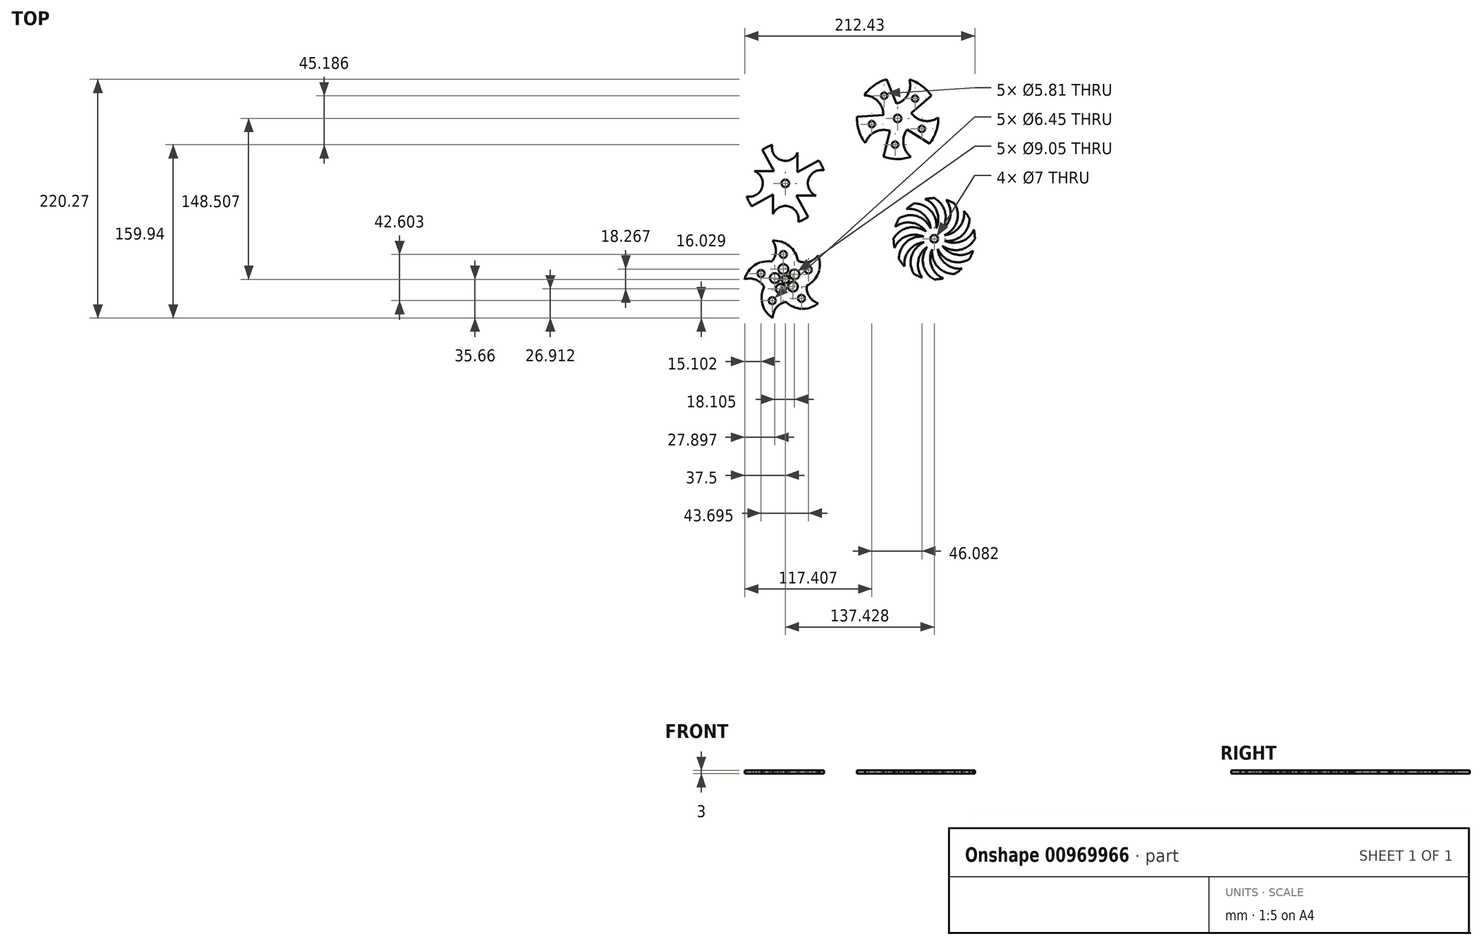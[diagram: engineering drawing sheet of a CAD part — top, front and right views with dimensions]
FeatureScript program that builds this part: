
annotation { "Feature Type Name" : "Feature", "Feature Type Description" : "" }
export const myFeature = defineFeature(function(context is Context, id is Id, definition is map)
    precondition{}
    {
        {
            var Q0;
            Q0=qCreatedBy(makeId("Top.planeOp"),FACE);
            var sketch = newSketch(context, id + "F0", { "sketchPlane" : qUnion([Q0])});
            skLineSegment(sketch, "E0.bottom", {"start": v(37.5, -37.5) * mm, "end": v(-37.5, -37.5) * mm});
            skLineSegment(sketch, "E0.top", {"start": v(37.5, 37.5) * mm, "end": v(-37.5, 37.5) * mm});
            skLineSegment(sketch, "E0.left", {"start": v(37.5, -37.5) * mm, "end": v(37.5, 37.5) * mm});
            skLineSegment(sketch, "E0.right", {"start": v(-37.5, -37.5) * mm, "end": v(-37.5, 37.5) * mm});
            skPoint(sketch, "E0.middle", {"position": v(0, 0) * mm});
            skCircle(sketch, "E1", {"center": v(0, 0) * mm, "radius": 3.5 * mm});
            skCircle(sketch, "E2", {"center": v(0, 0) * mm, "radius": 37.5 * mm});
            skArc(sketch, "E3", {"start": v(-12.52, 16.37) * mm, "mid": v(-28.22, 13.08) * mm, "end": v(-37.5, 0) * mm});
            skArc(sketch, "E4", {"start": v(-20.17, -5.87) * mm, "mid": v(-27.84, -0.01) * mm, "end": v(-37.5, 0) * mm});
            skArc(sketch, "E5", {"start": v(-20.17, -5.87) * mm, "mid": v(-19.82, -6.37) * mm, "end": v(-19.44, -6.85) * mm});
            skCircle(sketch, "E6", {"center": v(-9.6, 1.25) * mm, "radius": 4.53 * mm});
            skCircle(sketch, "E7", {"center": v(-22.4, 5.4) * mm, "radius": 3.23 * mm});
            skArc(sketch, "E8.1.0", {"start": v(-0.65, -21) * mm, "mid": v(-8.6, -26.48) * mm, "end": v(-11.59, -35.66) * mm});
            skArc(sketch, "E8.1.1", {"start": v(-19.44, -6.85) * mm, "mid": v(-21.16, -22.8) * mm, "end": v(-11.59, -35.66) * mm});
            skArc(sketch, "E8.1.2", {"start": v(-0.65, -21) * mm, "mid": v(-0.06, -20.81) * mm, "end": v(0.51, -20.6) * mm});
            skCircle(sketch, "E8.1.3", {"center": v(-12.06, -19.63) * mm, "radius": 3.23 * mm});
            skCircle(sketch, "E8.1.4", {"center": v(-4.15, -8.75) * mm, "radius": 4.53 * mm});
            skArc(sketch, "E8.2.0", {"start": v(19.77, -7.1) * mm, "mid": v(22.53, -16.36) * mm, "end": v(30.34, -22.04) * mm});
            skArc(sketch, "E8.2.1", {"start": v(0.51, -20.6) * mm, "mid": v(15.14, -27.17) * mm, "end": v(30.34, -22.04) * mm});
            skArc(sketch, "E8.2.2", {"start": v(19.77, -7.1) * mm, "mid": v(19.78, -6.5) * mm, "end": v(19.75, -5.88) * mm});
            skCircle(sketch, "E8.2.3", {"center": v(14.94, -17.54) * mm, "radius": 3.23 * mm});
            skCircle(sketch, "E8.2.4", {"center": v(7.04, -6.65) * mm, "radius": 4.53 * mm});
            skArc(sketch, "E8.3.0", {"start": v(12.86, 16.6) * mm, "mid": v(22.52, 16.38) * mm, "end": v(30.34, 22.04) * mm});
            skArc(sketch, "E8.3.1", {"start": v(19.75, -5.88) * mm, "mid": v(30.52, 6) * mm, "end": v(30.34, 22.04) * mm});
            skArc(sketch, "E8.3.2", {"start": v(12.86, 16.6) * mm, "mid": v(12.29, 16.8) * mm, "end": v(11.7, 16.97) * mm});
            skCircle(sketch, "E8.3.3", {"center": v(21.3, 8.8) * mm, "radius": 3.23 * mm});
            skCircle(sketch, "E8.3.4", {"center": v(8.5, 4.64) * mm, "radius": 4.53 * mm});
            skArc(sketch, "E8.4.0", {"start": v(-11.82, 17.37) * mm, "mid": v(-8.62, 26.48) * mm, "end": v(-11.59, 35.66) * mm});
            skArc(sketch, "E8.4.1", {"start": v(11.7, 16.97) * mm, "mid": v(3.72, 30.88) * mm, "end": v(-11.59, 35.66) * mm});
            skArc(sketch, "E8.4.2", {"start": v(-11.82, 17.37) * mm, "mid": v(-12.18, 16.88) * mm, "end": v(-12.52, 16.37) * mm});
            skCircle(sketch, "E8.4.3", {"center": v(-1.78, 22.97) * mm, "radius": 3.23 * mm});
            skCircle(sketch, "E8.4.4", {"center": v(-1.78, 9.52) * mm, "radius": 4.53 * mm});
            skPoint(sketch, "E9.orphan", {"position": v(-16.02, -2.03) * mm});
            skPoint(sketch, "E10.orphan", {"position": v(-6.88, 14.61) * mm});
            skPoint(sketch, "E11.orphan", {"position": v(-3.02, -15.87) * mm});
            skPoint(sketch, "E12.orphan", {"position": v(-0.8, 13.34) * mm});
            skPoint(sketch, "E13.orphan", {"position": v(12.44, 4.89) * mm});
            skPoint(sketch, "E14.orphan", {"position": v(14.16, -7.77) * mm});
            skPoint(sketch, "E15.orphan", {"position": v(11.77, 11.06) * mm});
            skSolve(sketch);
        }
        {
            var Q0;
            Q0=makeQuery(id+"F0.imprint","IMPRINT",FACE,{"disambiguationData":[TD([[makeQuery(id+"F0.imprint","IMPRINT",EDGE,{"derivedFrom":sQuery(id+"F0.wireOp",EDGE,"E1")}),-1.0]])]});
            extrude(context, id + "F1", {"entities" : qUnion([Q0]), "depth" : 3 * mm, "offsetDistance" : 25 * mm});
        }
        {
            var Q0;
            Q0=qCreatedBy(makeId("Top.planeOp"),FACE);
            var sketch = newSketch(context, id + "F2", { "sketchPlane" : qUnion([Q0])});
            skLineSegment(sketch, "E16.bottom", {"start": v(37.5, 126.08) * mm, "end": v(-37.5, 126.08) * mm});
            skLineSegment(sketch, "E16.top", {"start": v(37.5, 51.08) * mm, "end": v(-37.5, 51.08) * mm});
            skLineSegment(sketch, "E16.left", {"start": v(37.5, 126.08) * mm, "end": v(37.5, 51.08) * mm});
            skLineSegment(sketch, "E16.right", {"start": v(-37.5, 126.08) * mm, "end": v(-37.5, 51.08) * mm});
            skPoint(sketch, "E16.middle", {"position": v(0, 88.58) * mm});
            skCircle(sketch, "E17", {"center": v(0, 88.58) * mm, "radius": 37.5 * mm});
            skCircle(sketch, "E18", {"center": v(0, 88.58) * mm, "radius": 3.5 * mm});
            skArc(sketch, "E19", {"start": v(-12.02, 124.1) * mm, "mid": v(-3.55, 109.91) * mm, "end": v(11.36, 117.03) * mm});
            skLineSegment(sketch, "E20", {"start": v(-21.16, 119.54) * mm, "end": v(-10.3, 99.94) * mm});
            skLineSegment(sketch, "E21", {"start": v(-10.3, 99.94) * mm, "end": v(-28.45, 99.94) * mm});
            skArc(sketch, "E22.1.0", {"start": v(-35.52, 76.56) * mm, "mid": v(-21.33, 85.03) * mm, "end": v(-28.45, 99.94) * mm});
            skLineSegment(sketch, "E22.1.1", {"start": v(-30.96, 67.42) * mm, "end": v(-11.36, 78.28) * mm});
            skLineSegment(sketch, "E22.1.2", {"start": v(-11.36, 78.28) * mm, "end": v(-11.36, 60.13) * mm});
            skArc(sketch, "E22.2.0", {"start": v(12.02, 53.06) * mm, "mid": v(3.55, 67.25) * mm, "end": v(-11.36, 60.13) * mm});
            skLineSegment(sketch, "E22.2.1", {"start": v(21.16, 57.62) * mm, "end": v(10.3, 77.22) * mm});
            skLineSegment(sketch, "E22.2.2", {"start": v(10.3, 77.22) * mm, "end": v(28.45, 77.22) * mm});
            skArc(sketch, "E22.3.0", {"start": v(35.52, 100.6) * mm, "mid": v(21.33, 92.13) * mm, "end": v(28.45, 77.22) * mm});
            skLineSegment(sketch, "E22.3.1", {"start": v(30.96, 109.74) * mm, "end": v(11.36, 98.88) * mm});
            skLineSegment(sketch, "E22.3.2", {"start": v(11.36, 98.88) * mm, "end": v(11.36, 117.03) * mm});
            skPoint(sketch, "E23.orphan", {"position": v(11.36, 124.32) * mm});
            skPoint(sketch, "E24.orphan", {"position": v(12.02, 124.1) * mm});
            skPoint(sketch, "E25.orphan", {"position": v(35.52, 76.56) * mm});
            skPoint(sketch, "E26.orphan", {"position": v(35.74, 77.22) * mm});
            skPoint(sketch, "E27.orphan", {"position": v(-11.36, 52.84) * mm});
            skPoint(sketch, "E28.orphan", {"position": v(-12.02, 53.06) * mm});
            skPoint(sketch, "E29.orphan", {"position": v(-35.74, 99.94) * mm});
            skPoint(sketch, "E30.orphan", {"position": v(-35.52, 100.6) * mm});
            skSolve(sketch);
        }
        {
            var Q0;
            Q0=makeQuery(id+"F2.imprint","IMPRINT",FACE,{"disambiguationData":[TD([[makeQuery(id+"F2.imprint","IMPRINT",EDGE,{"derivedFrom":sQuery(id+"F2.wireOp",EDGE,"E18")}),-1.0]])]});
            extrude(context, id + "F3", {"entities" : qUnion([Q0]), "depth" : 3 * mm, "offsetDistance" : 25 * mm});
        }
        {
            var Q0;
            Q0=qCreatedBy(makeId("Top.planeOp"),FACE);
            var sketch = newSketch(context, id + "F4", { "sketchPlane" : qUnion([Q0])});
            skLineSegment(sketch, "E31.bottom", {"start": v(174.93, 0) * mm, "end": v(99.93, 0) * mm});
            skLineSegment(sketch, "E31.top", {"start": v(174.93, 75) * mm, "end": v(99.93, 75) * mm});
            skLineSegment(sketch, "E31.left", {"start": v(174.93, 0) * mm, "end": v(174.93, 75) * mm});
            skLineSegment(sketch, "E31.right", {"start": v(99.93, 0) * mm, "end": v(99.93, 75) * mm});
            skPoint(sketch, "E31.middle", {"position": v(137.43, 37.5) * mm});
            skCircle(sketch, "E32", {"center": v(137.43, 37.5) * mm, "radius": 37.5 * mm});
            skCircle(sketch, "E33", {"center": v(137.43, 37.5) * mm, "radius": 3.5 * mm});
            skArc(sketch, "E34", {"start": v(143.88, 45.04) * mm, "mid": v(147.57, 61.5) * mm, "end": v(137.43, 75) * mm});
            skArc(sketch, "E35", {"start": v(143.88, 45.04) * mm, "mid": v(152.21, 58.2) * mm, "end": v(148.47, 73.34) * mm});
            skArc(sketch, "E36.1.0", {"start": v(139.25, 47.25) * mm, "mid": v(134.2, 63.36) * mm, "end": v(118.68, 69.98) * mm});
            skArc(sketch, "E36.1.1", {"start": v(139.25, 47.25) * mm, "mid": v(139.88, 62.82) * mm, "end": v(129.07, 74.06) * mm});
            skArc(sketch, "E36.2.0", {"start": v(134.13, 46.85) * mm, "mid": v(121.7, 58.28) * mm, "end": v(104.95, 56.25) * mm});
            skArc(sketch, "E36.2.1", {"start": v(134.13, 46.85) * mm, "mid": v(126.89, 60.66) * mm, "end": v(111.91, 64.98) * mm});
            skArc(sketch, "E36.3.0", {"start": v(129.9, 43.95) * mm, "mid": v(113.42, 47.64) * mm, "end": v(99.93, 37.5) * mm});
            skArc(sketch, "E36.3.1", {"start": v(129.9, 43.95) * mm, "mid": v(116.72, 52.28) * mm, "end": v(101.6, 48.54) * mm});
            skArc(sketch, "E36.4.0", {"start": v(127.68, 39.32) * mm, "mid": v(111.57, 34.28) * mm, "end": v(104.95, 18.75) * mm});
            skArc(sketch, "E36.4.1", {"start": v(127.68, 39.32) * mm, "mid": v(112.1, 39.95) * mm, "end": v(100.87, 29.14) * mm});
            skArc(sketch, "E36.5.0", {"start": v(128.07, 34.2) * mm, "mid": v(116.65, 21.78) * mm, "end": v(118.68, 5.02) * mm});
            skArc(sketch, "E36.5.1", {"start": v(128.07, 34.2) * mm, "mid": v(114.27, 26.96) * mm, "end": v(109.95, 11.99) * mm});
            skArc(sketch, "E36.6.0", {"start": v(130.98, 29.96) * mm, "mid": v(127.3, 13.5) * mm, "end": v(137.43, 0) * mm});
            skArc(sketch, "E36.6.1", {"start": v(130.98, 29.96) * mm, "mid": v(122.64, 16.8) * mm, "end": v(126.39, 1.66) * mm});
            skArc(sketch, "E36.7.0", {"start": v(135.6, 27.75) * mm, "mid": v(140.65, 11.64) * mm, "end": v(156.18, 5.02) * mm});
            skArc(sketch, "E36.7.1", {"start": v(135.6, 27.75) * mm, "mid": v(134.98, 12.18) * mm, "end": v(145.78, 0.94) * mm});
            skArc(sketch, "E36.8.0", {"start": v(140.73, 28.15) * mm, "mid": v(153.15, 16.72) * mm, "end": v(169.9, 18.75) * mm});
            skArc(sketch, "E36.8.1", {"start": v(140.73, 28.15) * mm, "mid": v(147.97, 14.34) * mm, "end": v(162.94, 10.02) * mm});
            skArc(sketch, "E36.9.0", {"start": v(144.96, 31.05) * mm, "mid": v(161.43, 27.36) * mm, "end": v(174.93, 37.5) * mm});
            skArc(sketch, "E36.9.1", {"start": v(144.96, 31.05) * mm, "mid": v(158.14, 22.72) * mm, "end": v(173.27, 26.46) * mm});
            skArc(sketch, "E36.10.0", {"start": v(147.18, 35.68) * mm, "mid": v(163.29, 40.72) * mm, "end": v(169.9, 56.25) * mm});
            skArc(sketch, "E36.10.1", {"start": v(147.18, 35.68) * mm, "mid": v(162.75, 35.05) * mm, "end": v(173.99, 45.86) * mm});
            skArc(sketch, "E36.11.0", {"start": v(146.78, 40.8) * mm, "mid": v(158.21, 53.22) * mm, "end": v(156.18, 69.98) * mm});
            skArc(sketch, "E36.11.1", {"start": v(146.78, 40.8) * mm, "mid": v(160.59, 48.04) * mm, "end": v(164.91, 63.01) * mm});
            skSolve(sketch);
        }
        {
            var Q0;
            Q0=makeQuery(id+"F4.imprint","IMPRINT",FACE,{"disambiguationData":[TD([[makeQuery(id+"F4.imprint","IMPRINT",EDGE,{"derivedFrom":sQuery(id+"F4.wireOp",EDGE,"E33")}),-1.0]])]});
            extrude(context, id + "F5", {"entities" : qUnion([Q0]), "depth" : 3 * mm, "offsetDistance" : 25 * mm});
        }
        {
            var Q0;
            Q0=qCreatedBy(makeId("Top.planeOp"),FACE);
            var sketch = newSketch(context, id + "F6", { "sketchPlane" : qUnion([Q0])});
            skLineSegment(sketch, "E37.bottom", {"start": v(141.16, 111) * mm, "end": v(66.16, 111) * mm});
            skLineSegment(sketch, "E37.top", {"start": v(141.16, 186) * mm, "end": v(66.16, 186) * mm});
            skLineSegment(sketch, "E37.left", {"start": v(141.16, 111) * mm, "end": v(141.16, 186) * mm});
            skLineSegment(sketch, "E37.right", {"start": v(66.16, 111) * mm, "end": v(66.16, 186) * mm});
            skPoint(sketch, "E37.middle", {"position": v(103.66, 148.5) * mm});
            skCircle(sketch, "E38", {"center": v(103.66, 148.5) * mm, "radius": 37.5 * mm});
            skCircle(sketch, "E39", {"center": v(103.66, 148.5) * mm, "radius": 3.5 * mm});
            skLineSegment(sketch, "E40", {"start": v(93.52, 184.61) * mm, "end": v(102.6, 162.02) * mm});
            skArc(sketch, "E41", {"start": v(102.6, 162.02) * mm, "mid": v(113.17, 170.76) * mm, "end": v(114.43, 184.43) * mm});
            skCircle(sketch, "E42", {"center": v(91.3, 169.47) * mm, "radius": 2.9 * mm});
            skLineSegment(sketch, "E43.1.0", {"start": v(66.2, 150.02) * mm, "end": v(90.49, 151.67) * mm});
            skArc(sketch, "E43.1.1", {"start": v(90.49, 151.67) * mm, "mid": v(85.44, 164.43) * mm, "end": v(72.83, 169.85) * mm});
            skCircle(sketch, "E43.1.2", {"center": v(79.9, 143.22) * mm, "radius": 2.9 * mm});
            skLineSegment(sketch, "E43.2.0", {"start": v(90.64, 113.34) * mm, "end": v(96.58, 136.95) * mm});
            skArc(sketch, "E43.2.1", {"start": v(96.58, 136.95) * mm, "mid": v(82.89, 136.1) * mm, "end": v(73.84, 125.78) * mm});
            skCircle(sketch, "E43.2.2", {"center": v(101.35, 124.28) * mm, "radius": 2.9 * mm});
            skLineSegment(sketch, "E43.3.0", {"start": v(133.09, 125.26) * mm, "end": v(112.46, 138.2) * mm});
            skArc(sketch, "E43.3.1", {"start": v(112.46, 138.2) * mm, "mid": v(109.05, 124.91) * mm, "end": v(116.06, 113.12) * mm});
            skCircle(sketch, "E43.3.2", {"center": v(125.99, 138.82) * mm, "radius": 2.9 * mm});
            skLineSegment(sketch, "E43.4.0", {"start": v(134.87, 169.3) * mm, "end": v(116.18, 153.7) * mm});
            skArc(sketch, "E43.4.1", {"start": v(116.18, 153.7) * mm, "mid": v(127.77, 146.34) * mm, "end": v(141.15, 149.36) * mm});
            skCircle(sketch, "E43.4.2", {"center": v(119.77, 166.75) * mm, "radius": 2.9 * mm});
            skSolve(sketch);
        }
        {
            var Q0;
            Q0=makeQuery(id+"F6.imprint","IMPRINT",FACE,{"disambiguationData":[TD([[makeQuery(id+"F6.imprint","IMPRINT",EDGE,{"derivedFrom":sQuery(id+"F6.wireOp",EDGE,"E39")}),-1.0]])]});
            extrude(context, id + "F7", {"entities" : qUnion([Q0]), "depth" : 3 * mm, "offsetDistance" : 25 * mm});
        }
    });
